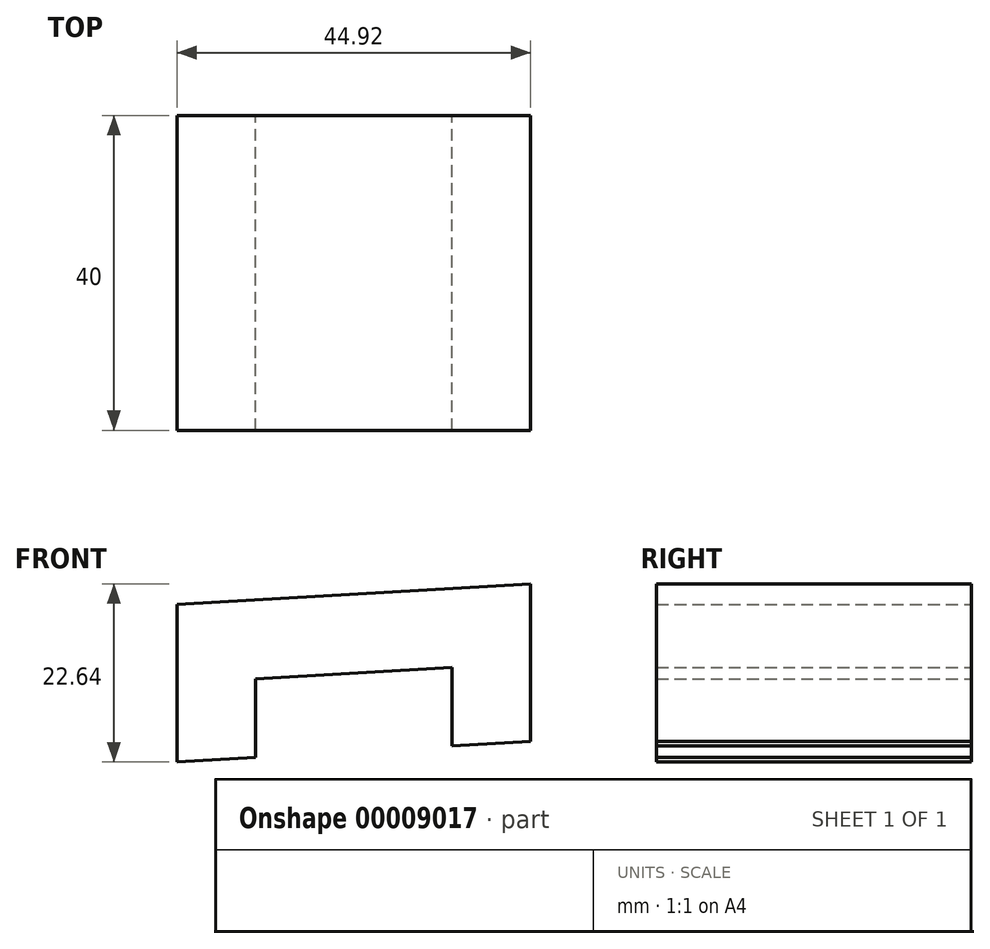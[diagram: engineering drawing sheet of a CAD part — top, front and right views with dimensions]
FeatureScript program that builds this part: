
annotation { "Feature Type Name" : "Feature", "Feature Type Description" : "" }
export const myFeature = defineFeature(function(context is Context, id is Id, definition is map)
    precondition{}
    {
        {
            var Q0;
            Q0=qCreatedBy(makeId("Front.planeOp"),FACE);
            var sketch = newSketch(context, id + "F0", { "sketchPlane" : qUnion([Q0])});
            skLineSegment(sketch, "E0.rect.bottom", {"start": v(22.46, 21.32) * mm, "end": v(-22.46, 18.68) * mm});
            skLineSegment(sketch, "E0.rect.left", {"start": v(22.46, 21.32) * mm, "end": v(22.46, 1.32) * mm});
            skLineSegment(sketch, "E0.rect.right", {"start": v(-22.46, 18.68) * mm, "end": v(-22.46, -1.32) * mm});
            skPoint(sketch, "E0.rect.middle", {"position": v(0, 0) * mm});
            skLineSegment(sketch, "E1.rect.bottom", {"start": v(12.46, 10.72) * mm, "end": v(-12.46, 9.25) * mm});
            skLineSegment(sketch, "E1.rect.left", {"start": v(12.46, 10.72) * mm, "end": v(12.46, 0.73) * mm});
            skLineSegment(sketch, "E1.rect.right", {"start": v(-12.46, 9.25) * mm, "end": v(-12.46, -0.73) * mm});
            skLineSegment(sketch, "E2", {"start": v(-22.46, -1.32) * mm, "end": v(-12.46, -0.73) * mm});
            skLineSegment(sketch, "E3", {"start": v(12.46, 0.73) * mm, "end": v(22.46, 1.32) * mm});
            skPoint(sketch, "E1.rect.top.end.orphan", {"position": v(-12.46, -10.72) * mm});
            skPoint(sketch, "E1.rect.top.start.orphan", {"position": v(12.46, -9.25) * mm});
            skPoint(sketch, "E0.rect.top.end.orphan", {"position": v(-22.46, -21.32) * mm});
            skPoint(sketch, "E0.rect.top.start.orphan", {"position": v(22.46, -18.68) * mm});
            skSolve(sketch);
        }
        {
            var Q0;
            Q0=qSketchRegion(id+"F0",true);
            extrude(context, id + "F1", {"entities" : qUnion([Q0]), "endBound" : BoundingType.SYMMETRIC, "depth" : 40 * mm});
        }
    });
